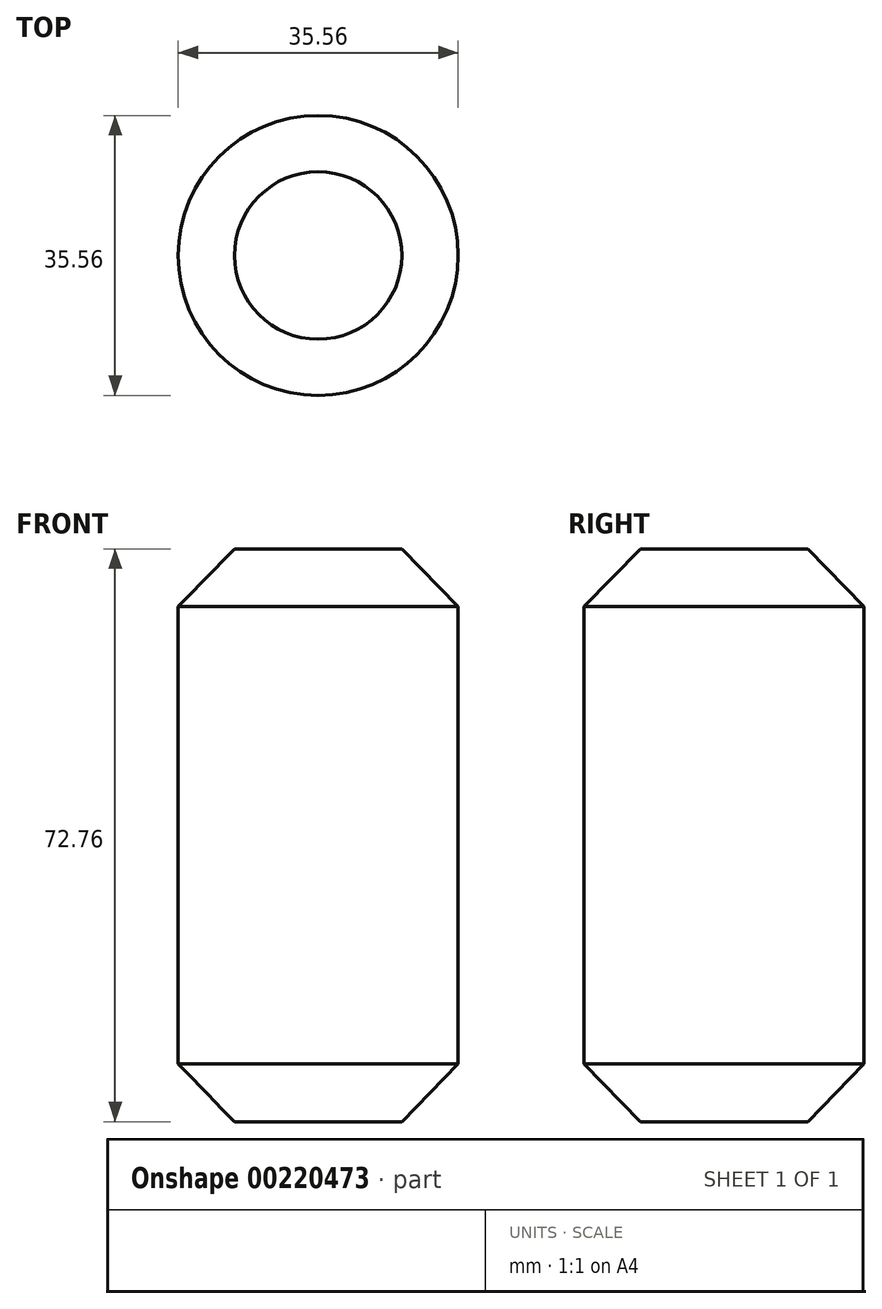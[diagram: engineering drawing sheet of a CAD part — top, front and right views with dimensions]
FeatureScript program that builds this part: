
annotation { "Feature Type Name" : "Feature", "Feature Type Description" : "" }
export const myFeature = defineFeature(function(context is Context, id is Id, definition is map)
    precondition{}
    {
        {
            var Q0;
            Q0=qCreatedBy(makeId("Front.planeOp"),FACE);
            var sketch = newSketch(context, id + "F0", { "sketchPlane" : qUnion([Q0])});
            skLineSegment(sketch, "E0.top", {"start": v(0, 36.38) * mm, "end": v(-10.63, 36.38) * mm});
            skLineSegment(sketch, "E0.left", {"start": v(0, 0) * mm, "end": v(0, 36.38) * mm});
            skLineSegment(sketch, "E0.right", {"start": v(-17.78, 0) * mm, "end": v(-17.78, 29.05) * mm});
            skLineSegment(sketch, "E1", {"start": v(-17.78, 29.05) * mm, "end": v(-10.63, 36.38) * mm});
            skLineSegment(sketch, "E2.MirrorCS", {"start": v(-17.78, 0) * mm, "end": v(-17.78, -29.05) * mm});
            skLineSegment(sketch, "E3.MirrorCS", {"start": v(-17.78, -29.05) * mm, "end": v(-10.63, -36.38) * mm});
            skLineSegment(sketch, "E4.MirrorCS", {"start": v(0, -36.38) * mm, "end": v(-10.63, -36.38) * mm});
            skLineSegment(sketch, "E5.MirrorCS", {"start": v(0, 0) * mm, "end": v(0, -36.38) * mm});
            skSolve(sketch);
        }
        {
            var Q0;
            Q0=makeQuery(id+"F0.imprint","IMPRINT",FACE,{"disambiguationData":[TD([[makeQuery(id+"F0.imprint","IMPRINT",EDGE,{"derivedFrom":sQuery(id+"F0.wireOp",EDGE,"E0.top")}),1.0]])]});
            var Q1;
            Q1=sQuery(id+"F0.wireOp",EDGE,"E0.left");
            revolve(context, id + "F1", {"entities" : qUnion([Q0]), "axis" : qUnion([Q1]), "revolveType" : RevolveType.FULL});
        }
    });
